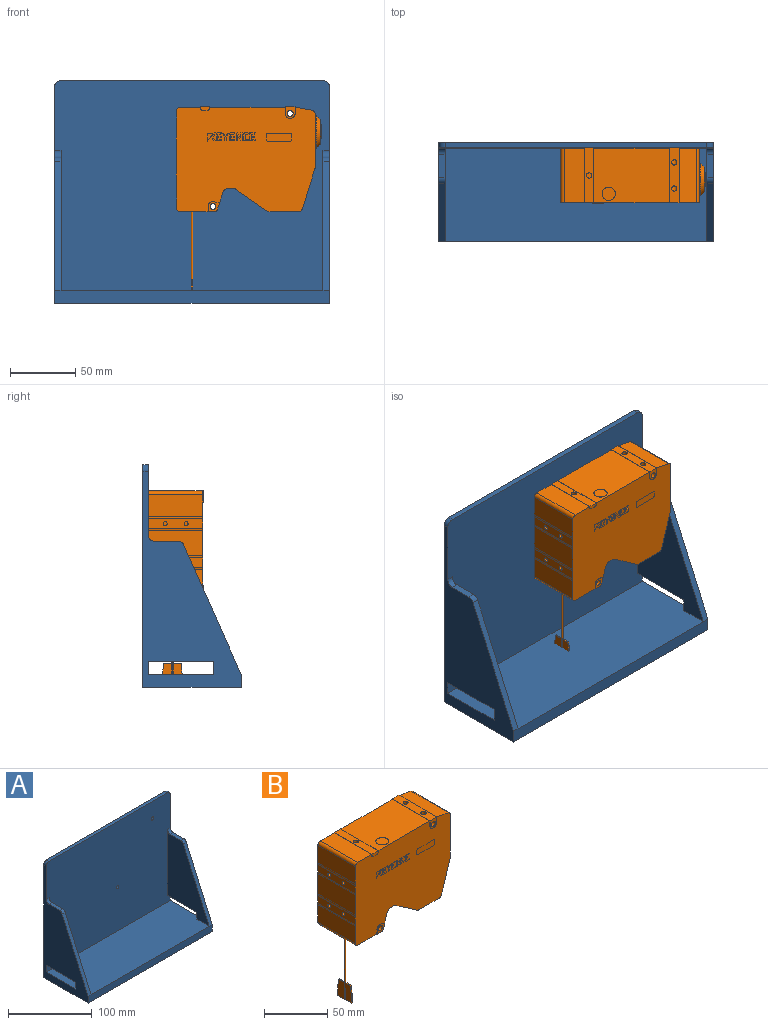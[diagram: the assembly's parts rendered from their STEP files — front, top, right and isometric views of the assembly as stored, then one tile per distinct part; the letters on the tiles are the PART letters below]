
ASSEMBLY  parts=2 mates=1
PART A: 26 faces, bbox 210x75x170 mm
  f0: plane 210x71mm, normal (0,0,1), area 14700mm2, adj f1,f3,f4,f5,f6,f11,f14,f16
  f1: plane 165x75mm, normal (1,0,0), area 5794.2mm2, adj f0,f6,f8,f11,f12,f15,f16,f17
  f2: plane 98.53x43.72mm, normal (0,-0.91,0.41), area 539mm2, adj f3,f4,f11,f23
  f3: plane 165x75mm, normal (-1,0,0), area 5794.2mm2, adj f0,f2,f6,f8,f11,f12,f13,f14
  f4: plane 106.5x71mm, normal (1,0,0), area 4424.2mm2, adj f0,f2,f6,f13,f14,f19,f22,f23
  f5: plane 106.5x71mm, normal (-1,0,0), area 4424.2mm2, adj f0,f6,f15,f16,f17,f18,f20,f21
  f6: plane 210x160mm, normal (0,-1,0), area 32593.9mm2, adj f0,f1,f3,f4,f5,f7,f9,f10
  f7: plane 200x4mm, normal (0,0,1), area 800mm2, adj f6,f8,f24,f25
  f8: plane 210x170mm, normal (0,1,0), area 35658.9mm2, adj f1,f3,f7,f9,f10,f12,f24,f25
  f9: cylinder r=2.2mm len=4.4mm, axis (0,-1,0), area 55.3mm2, adj f6,f8
  f10: cylinder r=2.2mm len=4.4mm, axis (0,-1,0), area 55.3mm2, adj f6,f8
  f11: plane 210x10mm, normal (0,-1,0), area 2100mm2, adj f0,f1,f2,f3,f12,f15
  f12: plane 210x75mm, normal (0,0,-1), area 15750mm2, adj f1,f3,f8,f11
  f13: plane 50x5mm, normal (0,0,-1), area 250mm2, adj f3,f4,f6,f14
  f14: plane 10x5mm, normal (0,1,0), area 50mm2, adj f0,f3,f4,f13
  f15: plane 98.53x43.72mm, normal (0,-0.91,0.41), area 539mm2, adj f1,f5,f11,f21
  f16: plane 10x5mm, normal (0,1,0), area 50mm2, adj f0,f1,f5,f17
  f17: plane 50x5mm, normal (0,0,-1), area 250mm2, adj f1,f5,f6,f16
  f18: plane 17.71x5mm, normal (0,0,1), area 88.5mm2, adj f1,f5,f20,f21
  f19: plane 17.71x5mm, normal (0,0,1), area 88.5mm2, adj f3,f4,f22,f23
  f20: cylinder r=5mm len=5mm, axis (-1,0,0), area 39.3mm2, adj f1,f5,f6,f18
  f21: cylinder r=5mm len=5mm, axis (1,0,0), area 28.8mm2, adj f1,f5,f15,f18
  f22: cylinder r=5mm len=5mm, axis (-1,0,0), area 39.3mm2, adj f3,f4,f6,f19
  f23: cylinder r=5mm len=5mm, axis (-1,0,0), area 28.8mm2, adj f2,f3,f4,f19
  f24: cylinder r=5mm len=5mm, axis (0,-1,0), area 31.4mm2, adj f1,f6,f7,f8
  f25: cylinder r=5mm len=5mm, axis (0,1,0), area 31.4mm2, adj f3,f6,f7,f8
PART B: 340 faces, bbox 111x42x148 mm
  f0: cone r=4.25mm half-angle=90deg, axis (-1,0,0), area 56.7mm2, adj f1
  f1: cylinder r=4.25mm len=8.5mm, axis (-1,0,0), area 106.8mm2, adj f0,f2
  f2: plane 9.5x9.5mm, normal (1,0,0), area 14.1mm2, adj f1,f10
  f3: plane 6.19x1mm, normal (0,0,1), area 6.1mm2, adj f4,f11,f12,f16
  f4: plane 8x1mm, normal (0,-1,0.09), area 8mm2, adj f3,f5,f11,f12
  f5: plane 8x1mm, normal (0,-1,0), area 8mm2, adj f4,f8,f11,f12
  f6: plane 8x1mm, normal (0,1,0.09), area 8mm2, adj f7,f9,f13,f14
  f7: plane 6.19x1mm, normal (0,0,1), area 6.1mm2, adj f6,f13,f14,f17
  f8: plane 15x1.5mm, normal (0,0,-1), area 15.4mm2, adj f5,f9,f11,f12,f13,f14,f16,f17
  f9: plane 8x1mm, normal (0,1,0), area 8mm2, adj f6,f8,f13,f14
  f10: cylinder r=4.75mm len=9.5mm, axis (-1,0,0), area 119.4mm2, adj f2,f15
  f11: plane 16x6.94mm, normal (1,0,0), area 108.1mm2, adj f3,f4,f5,f8,f16
  f12: plane 16x6.94mm, normal (-1,0,0), area 108.1mm2, adj f3,f4,f5,f8,f16
  f13: plane 16x6.94mm, normal (-1,0,0), area 108.1mm2, adj f6,f7,f8,f9,f17
  f14: plane 16x6.94mm, normal (1,0,0), area 108.1mm2, adj f6,f7,f8,f9,f17
  f15: plane 10.5x10.5mm, normal (1,0,0), area 15.7mm2, adj f10,f19
  f16: cylinder r=0.75mm len=68.1mm, axis (0,0,-1), area 142.9mm2, adj f3,f8,f11,f12,f17,f20
  f17: cylinder r=0.75mm len=68.1mm, axis (0,0,-1), area 142.9mm2, adj f7,f8,f13,f14,f16,f20
  f18: plane 16x13.11mm, normal (-0.57,0,-0.82), area 201.1mm2, adj f21
  f19: cone r=5.25mm half-angle=0deg, axis (1,0,0), area 131.9mm2, adj f15,f22
  f20: plane 15x3mm, normal (0,0,-1), area 43.2mm2, adj f16,f17,f23,f24,f25,f26
  f21: cylinder r=8mm len=16mm, axis (-0.57,0,-0.82), area 5mm2, adj f18,f27
  f22: cone r=8.5mm half-angle=90deg, axis (-1,0,0), area 140.4mm2, adj f19,f28
  f23: plane 15x0.1mm, normal (-1,0,0), area 1.5mm2, adj f20,f24,f26,f30
  f24: plane 3x0.1mm, normal (0,1,0), area 0.3mm2, adj f20,f23,f25,f30
  f25: plane 15x0.1mm, normal (1,0,0), area 1.5mm2, adj f20,f24,f26,f30
  f26: plane 3x0.1mm, normal (0,-1,0), area 0.3mm2, adj f20,f23,f25,f30
  f27: plane 19.8x16.22mm, normal (-0.57,0,-0.82), area 191mm2, adj f21,f31,f32,f33,f34
  f28: cylinder r=8.5mm len=17mm, axis (-1,0,0), area 160.2mm2, adj f22,f35
  f29: plane 4x4mm, normal (0,0,1), area 12.6mm2, adj f36
  f30: plane 19.8x13.8mm, normal (0,0,-1), area 228.2mm2, adj f23,f24,f25,f26,f37,f38,f39,f40
  f31: plane 19.8x0.08mm, normal (0.82,0,-0.57), area 2mm2, adj f27,f32,f34,f51
  f32: plane 16.28x11.44mm, normal (0,1,0), area 2mm2, adj f27,f31,f33,f51
  f33: plane 19.8x0.08mm, normal (-0.82,0,0.57), area 2mm2, adj f27,f32,f34,f51
  f34: plane 16.28x11.44mm, normal (0,-1,0), area 2mm2, adj f27,f31,f33,f51
  f35: plane 19x19mm, normal (1,0,0), area 56.5mm2, adj f28,f52
  f36: cylinder r=2mm len=4.2mm, axis (0,0,1), area 52.8mm2, adj f29,f57
  f37: plane 19.8x0.1mm, normal (1,0,0), area 2mm2, adj f30,f38,f40,f62
  f38: plane 13.8x0.1mm, normal (0,1,0), area 1.4mm2, adj f30,f37,f39,f62
  f39: plane 19.8x0.1mm, normal (-1,0,0), area 2mm2, adj f30,f38,f40,f62
  f40: plane 13.8x0.1mm, normal (0,-1,0), area 1.4mm2, adj f30,f37,f39,f62
  f41: plane 6.97x2.98mm, normal (0,-1,0), area 19.1mm2, adj f57,f66,f67,f68,f185,f189
  f42: plane 19.1x5.6mm, normal (0,-1,0), area 106.5mm2, adj f69,f70,f71,f72,f73,f74,f75,f76
  f43: plane 5.91x4.22mm, normal (0,-1,0), area 12.8mm2, adj f77,f78,f79,f80,f81,f82,f83,f84
  f44: plane 6.17x4.28mm, normal (0,-1,0), area 12.9mm2, adj f89,f90,f91,f92
  f45: plane 5.92x4.29mm, normal (0,-1,0), area 16mm2, adj f93,f94,f95,f96,f97,f98,f99,f100
  f46: plane 5.92x4.29mm, normal (0,-1,0), area 16mm2, adj f109,f110,f111,f112,f113,f114,f115,f116
  f47: plane 5.96x4.36mm, normal (0,-1,0), area 16.6mm2, adj f125,f126,f127,f128,f129,f130,f131,f132
  f48: plane 5.9x3.51mm, normal (0,-1,0), area 8mm2, adj f141,f142,f143,f144,f145,f146
  f49: plane 5.91x4.97mm, normal (0,-1,0), area 8.9mm2, adj f147,f148,f149,f150,f151,f152,f153,f154
  f50: plane 5.91x4.74mm, normal (0,-1,0), area 18.3mm2, adj f156,f157,f158,f159,f160,f161,f162,f163
  f51: plane 20x16.38mm, normal (-0.57,0,-0.82), area 8mm2, adj f31,f32,f33,f34,f174,f175,f176,f177
  f52: cone r=12.5mm half-angle=45deg, axis (-1,0,0), area 293.2mm2, adj f35,f179
  f53: cylinder r=2mm len=4.08mm, axis (0,0,1), area 42.4mm2, adj f55,f181
  f54: cylinder r=2mm len=4.08mm, axis (0,0,1), area 42.4mm2, adj f55,f181
  f55: cylinder r=2.2mm len=42mm, axis (0,1,0), area 551.2mm2, adj f53,f54,f182,f184
  f56: plane 10.12x10.12mm, normal (0,0,1), area 80.4mm2, adj f187
  f57: plane 42x6.97mm, normal (0,0,1), area 280mm2, adj f36,f41,f185,f188,f189
  f58: plane 3x3mm, normal (-1,0,0), area 7.1mm2, adj f191
  f59: plane 3x3mm, normal (-1,0,0), area 7.1mm2, adj f192
  f60: plane 3x3mm, normal (-1,0,0), area 7.1mm2, adj f195
  f61: plane 3x3mm, normal (-1,0,0), area 7.1mm2, adj f196
  f62: plane 20x14mm, normal (0,0,-1), area 6.8mm2, adj f37,f38,f39,f40,f198,f199,f200,f201
  f63: cylinder r=3.73mm len=7.47mm, axis (0,1,0), area 2.3mm2, adj f64,f182,f202,f258
  f64: plane 4.8x0.2mm, normal (-1,0,0), area 1mm2, adj f63,f65,f182,f202
  f65: plane 0.2x0mm, normal (0,0,-1), area 0mm2, adj f64,f182,f186,f202
  f66: cylinder r=1.98mm len=1.98mm, axis (0,1,0), area 0.6mm2, adj f41,f67,f185,f202
  f67: plane 3x0.2mm, normal (0,0,-1), area 0.6mm2, adj f41,f66,f68,f202
  f68: cylinder r=1.98mm len=1.98mm, axis (0,1,0), area 0.6mm2, adj f41,f67,f189,f202
  f69: cylinder r=0.7mm len=0.7mm, axis (0,-1,0), area 0mm2, adj f42,f70,f76,f202
  f70: plane 17.7x0.01mm, normal (0,0,-1), area 0.2mm2, adj f42,f69,f71,f202
  f71: cylinder r=0.7mm len=0.7mm, axis (0,-1,0), area 0mm2, adj f42,f70,f72,f202
  f72: plane 4.2x0.01mm, normal (-1,0,0), area 0mm2, adj f42,f71,f73,f202
  f73: cylinder r=0.7mm len=0.7mm, axis (0,-1,0), area 0mm2, adj f42,f72,f74,f202
  f74: plane 17.7x0.01mm, normal (0,0,1), area 0.2mm2, adj f42,f73,f75,f202
  f75: cylinder r=0.7mm len=0.7mm, axis (0,-1,0), area 0mm2, adj f42,f74,f76,f202
  f76: plane 4.2x0.01mm, normal (1,0,0), area 0mm2, adj f42,f69,f75,f202
  f77: extruded ~0.48x0.26mm, area 0mm2, adj f43,f78,f88,f202
  f78: plane 2.6x0.01mm, normal (1,0,0), area 0mm2, adj f43,f77,f79,f202
  f79: extruded ~0.48x0.26mm, area 0mm2, adj f43,f78,f80,f202
  f80: plane 2.78x0.01mm, normal (0,0,1), area 0mm2, adj f43,f79,f81,f202
  f81: plane 1.17x0.01mm, normal (1,0,0), area 0mm2, adj f43,f80,f82,f202
  f82: plane 3.35x0.01mm, normal (0,0,-1), area 0mm2, adj f43,f81,f83,f202
  f83: extruded ~1.51x0.82mm, area 0mm2, adj f43,f82,f84,f202
  f84: plane 2.89x0.01mm, normal (-1,0,0), area 0mm2, adj f43,f83,f85,f202
  f85: extruded ~1.5x0.82mm, area 0mm2, adj f43,f84,f86,f202
  f86: plane 3.4x0.01mm, normal (0,0,1), area 0mm2, adj f43,f85,f87,f202
  f87: cylinder r=2846.98mm len=1.16mm, axis (0,1,0), area 0mm2, adj f43,f86,f88,f202
  f88: plane 1.95x0.01mm, normal (0,0,-1), area 0mm2, adj f43,f77,f87,f202
  f89: extruded ~1.5x0.82mm, area 0mm2, adj f44,f90,f92,f202
  f90: plane 3.45x0.01mm, normal (0,0,1), area 0mm2, adj f44,f89,f91,f202
  f91: extruded ~6.17x4.27mm, area 0.1mm2, adj f44,f90,f92,f202
  f92: plane 4.66x0.01mm, normal (-1,0,0), area 0mm2, adj f44,f89,f91,f202
  f93: extruded ~1.5x0.82mm, area 0mm2, adj f45,f94,f108,f202
  f94: plane 3.47x0.01mm, normal (0,0,1), area 0mm2, adj f45,f93,f95,f202
  f95: cylinder r=2856.37mm len=1.16mm, axis (0,1,0), area 0mm2, adj f45,f94,f96,f202
  f96: plane 1.98x0.01mm, normal (0,0,-1), area 0mm2, adj f45,f95,f97,f202
  f97: extruded ~0.48x0.26mm, area 0mm2, adj f45,f96,f98,f202
  f98: plane 0.81x0.01mm, normal (1,0,0), area 0mm2, adj f45,f97,f99,f202
  f99: plane 2.84x0.01mm, normal (0,0,1), area 0mm2, adj f45,f98,f100,f202
  f100: plane 0.99x0.01mm, normal (1,0,0), area 0mm2, adj f45,f99,f101,f202
  f101: plane 2.84x0.01mm, normal (0,0,-1), area 0mm2, adj f45,f100,f102,f202
  f102: plane 0.81x0.01mm, normal (1,0,0), area 0mm2, adj f45,f101,f103,f202
  f103: extruded ~0.5x0.27mm, area 0mm2, adj f45,f102,f104,f202
  f104: plane 2.8x0.01mm, normal (0,0,1), area 0mm2, adj f45,f103,f105,f202
  f105: plane 1.16x0.01mm, normal (1,0,0), area 0mm2, adj f45,f104,f106,f202
  f106: plane 3.44x0.01mm, normal (0,0,-1), area 0mm2, adj f45,f105,f107,f202
  f107: extruded ~1.5x0.81mm, area 0mm2, adj f45,f106,f108,f202
  f108: plane 2.9x0.01mm, normal (-1,0,0), area 0mm2, adj f45,f93,f107,f202
  f109: extruded ~0.5x0.27mm, area 0mm2, adj f46,f110,f124,f202
  f110: plane 2.8x0.01mm, normal (0,0,1), area 0mm2, adj f46,f109,f111,f202
  f111: plane 1.16x0.01mm, normal (1,0,0), area 0mm2, adj f46,f110,f112,f202
  f112: plane 3.44x0.01mm, normal (0,0,-1), area 0mm2, adj f46,f111,f113,f202
  f113: extruded ~1.5x0.81mm, area 0mm2, adj f46,f112,f114,f202
  f114: plane 2.9x0.01mm, normal (-1,0,0), area 0mm2, adj f46,f113,f115,f202
  f115: extruded ~1.5x0.82mm, area 0mm2, adj f46,f114,f116,f202
  f116: plane 3.47x0.01mm, normal (0,0,1), area 0mm2, adj f46,f115,f117,f202
  f117: cylinder r=2855.24mm len=1.16mm, axis (0,1,0), area 0mm2, adj f46,f116,f118,f202
  f118: plane 1.98x0.01mm, normal (0,0,-1), area 0mm2, adj f46,f117,f119,f202
  f119: extruded ~0.48x0.26mm, area 0mm2, adj f46,f118,f120,f202
  f120: plane 0.81x0.01mm, normal (1,0,0), area 0mm2, adj f46,f119,f121,f202
  f121: plane 2.84x0.01mm, normal (0,0,1), area 0mm2, adj f46,f120,f122,f202
  f122: plane 0.99x0.01mm, normal (1,0,0), area 0mm2, adj f46,f121,f123,f202
  f123: plane 2.84x0.01mm, normal (0,0,-1), area 0mm2, adj f46,f122,f124,f202
  f124: plane 0.81x0.01mm, normal (1,0,0), area 0mm2, adj f46,f109,f123,f202
  f125: extruded ~1.53x0.84mm, area 0mm2, adj f47,f126,f140,f202
  f126: plane 3.51x0.01mm, normal (0,0,1), area 0mm2, adj f47,f125,f127,f202
  f127: cylinder r=2853.49mm len=1.2mm, axis (0,1,0), area 0mm2, adj f47,f126,f128,f202
  f128: plane 1.99x0.01mm, normal (0,0,-1), area 0mm2, adj f47,f127,f129,f202
  f129: extruded ~0.46x0.24mm, area 0mm2, adj f47,f128,f130,f202
  f130: plane 0.78x0.01mm, normal (1,0,0), area 0mm2, adj f47,f129,f131,f202
  f131: plane 2.84x0.01mm, normal (0,0,1), area 0mm2, adj f47,f130,f132,f202
  f132: plane 1.03x0.01mm, normal (1,0,0), area 0mm2, adj f47,f131,f133,f202
  f133: plane 2.84x0.01mm, normal (0,0,-1), area 0mm2, adj f47,f132,f134,f202
  f134: plane 0.79x0.01mm, normal (1,0,0), area 0mm2, adj f47,f133,f135,f202
  f135: extruded ~0.48x0.25mm, area 0mm2, adj f47,f134,f136,f202
  f136: plane 2.83x0.01mm, normal (0,0,1), area 0mm2, adj f47,f135,f137,f202
  f137: plane 1.2x0.01mm, normal (1,0,0), area 0mm2, adj f47,f136,f138,f202
  f138: plane 3.46x0.01mm, normal (0,0,-1), area 0mm2, adj f47,f137,f139,f202
  f139: extruded ~1.53x0.84mm, area 0mm2, adj f47,f138,f140,f202
  f140: plane 2.9x0.01mm, normal (-1,0,0), area 0mm2, adj f47,f125,f139,f202
  f141: plane 1.32x0.01mm, normal (0,0,1), area 0mm2, adj f48,f142,f146,f202
  f142: cylinder r=2917.35mm len=2.86mm, axis (0,1,0), area 0mm2, adj f48,f141,f143,f202
  f143: cylinder r=3224.09mm len=3.04mm, axis (0,-1,0), area 0mm2, adj f48,f142,f144,f202
  f144: plane 1.37x0.01mm, normal (0,0,-1), area 0mm2, adj f48,f143,f145,f202
  f145: cylinder r=3203.54mm len=2.96mm, axis (0,1,0), area 0mm2, adj f48,f144,f146,f202
  f146: cylinder r=2923.49mm len=2.95mm, axis (0,-1,0), area 0mm2, adj f48,f141,f145,f202
  f147: plane 2.87x0.01mm, normal (-1,0,0), area 0mm2, adj f49,f148,f155,f202
  f148: cylinder r=2953.73mm len=3.04mm, axis (0,1,0), area 0mm2, adj f49,f147,f149,f202
  f149: plane 0.97x0.01mm, normal (0,0,1), area 0mm2, adj f49,f148,f150,f202
  f150: cylinder r=2922.38mm len=2.34mm, axis (0,-1,0), area 0mm2, adj f49,f149,f151,f202
  f151: cylinder r=2921.52mm len=2.34mm, axis (0,-1,0), area 0mm2, adj f49,f150,f152,f202
  f152: plane 0.97x0.01mm, normal (0,0,1), area 0mm2, adj f49,f151,f153,f202
  f153: cylinder r=2953.58mm len=3.04mm, axis (0,1,0), area 0mm2, adj f49,f152,f154,f202
  f154: plane 2.87x0.01mm, normal (1,0,0), area 0mm2, adj f49,f153,f155,f202
  f155: plane 1.11x0.01mm, normal (0,0,-1), area 0mm2, adj f49,f147,f154,f202
  f156: plane 3.55x0.01mm, normal (-1,0,0), area 0mm2, adj f50,f157,f165,f202
  f157: plane 1.12x0.01mm, normal (0,0,1), area 0mm2, adj f50,f156,f158,f202
  f158: plane 5.91x0.01mm, normal (1,0,0), area 0.1mm2, adj f50,f157,f159,f202
  f159: plane 1.02x0.01mm, normal (0,0,-1), area 0mm2, adj f50,f158,f160,f202
  f160: cylinder r=3134.07mm len=3.98mm, axis (0,1,0), area 0mm2, adj f50,f159,f161,f202
  f161: plane 3.99x0.01mm, normal (1,0,0), area 0mm2, adj f50,f160,f162,f202
  f162: plane 1.12x0.01mm, normal (0,0,-1), area 0mm2, adj f50,f161,f163,f202
  f163: plane 5.91x0.01mm, normal (-1,0,0), area 0.1mm2, adj f50,f162,f164,f202
  f164: plane 1.09x0.01mm, normal (0,0,1), area 0mm2, adj f50,f163,f165,f202
  f165: cylinder r=2944.12mm len=3.55mm, axis (0,-1,0), area 0mm2, adj f50,f156,f164,f202
  f166: plane 3.81x1.2mm, normal (0.3,0,0.95), area 0.8mm2, adj f167,f202,f203,f247
  f167: cylinder r=3.73mm len=4.86mm, axis (0,1,0), area 1.4mm2, adj f166,f168,f202,f203
  f168: plane 4x0.2mm, normal (-1,0,0), area 0.8mm2, adj f167,f202,f203,f274
  f169: cylinder r=2.2mm len=42mm, axis (0,1,0), area 580.6mm2, adj f203,f205
  f170: plane 5.96x4.36mm, normal (0,1,0), area 16.6mm2, adj f211,f212,f213,f214,f215,f216,f217,f218
  f171: plane 5.9x3.51mm, normal (0,1,0), area 8mm2, adj f227,f228,f229,f230,f231,f232
  f172: plane 6.17x4.28mm, normal (0,1,0), area 12.9mm2, adj f233,f234,f235,f236
  f173: plane 19.1x5.6mm, normal (0,1,0), area 106.5mm2, adj f237,f238,f239,f240,f241,f242,f243,f244
  f174: plane 20x0.08mm, normal (-0.82,0,0.57), area 2mm2, adj f51,f175,f177,f251
  f175: plane 16.44x11.55mm, normal (0,1,0), area 2mm2, adj f51,f174,f176,f251
  f176: plane 20x0.08mm, normal (0.82,0,-0.57), area 2mm2, adj f51,f175,f177,f251
  f177: plane 16.44x11.55mm, normal (0,-1,0), area 2mm2, adj f51,f174,f176,f251
  f178: cylinder r=2.7mm len=41.6mm, axis (0,1,0), area 68.6mm2, adj f202,f251,f252,f339
  f179: cylinder r=12.5mm len=25mm, axis (-1,0,0), area 78.5mm2, adj f52,f255
  f180: cylinder r=2.7mm len=41.6mm, axis (0,1,0), area 34.3mm2, adj f202,f254,f255,f339
  f181: plane 42x7.47mm, normal (0,0,1), area 288.5mm2, adj f53,f54,f182,f184,f186,f258
  f182: plane 8.73x7.47mm, normal (0,-1,0), area 44mm2, adj f55,f63,f64,f65,f181,f186,f258
  f183: plane 41.6x0.02mm, normal (0,0,1), area 0.7mm2, adj f202,f257,f258,f339
  f184: plane 8.73x7.47mm, normal (0,1,0), area 44mm2, adj f55,f181,f186,f258,f259,f260,f261
  f185: plane 42x1mm, normal (1,0,0), area 8.7mm2, adj f41,f57,f66,f188,f202,f262,f263,f339
  f186: plane 42x0.2mm, normal (-1,0,0), area 8.4mm2, adj f65,f181,f182,f184,f261,f262
  f187: cylinder r=5.06mm len=10.12mm, axis (0,0,1), area 3.2mm2, adj f56,f262
  f188: plane 6.97x2.98mm, normal (0,1,0), area 19.1mm2, adj f57,f185,f189,f263,f264,f265
  f189: plane 42x1mm, normal (-1,0,0), area 8.7mm2, adj f41,f57,f68,f188,f202,f265,f266,f339
  f190: cylinder r=5.91mm len=41.6mm, axis (0,1,0), area 64.7mm2, adj f202,f268,f269,f339
  f191: cylinder r=1.5mm len=3.5mm, axis (-1,0,0), area 33mm2, adj f58,f269
  f192: cylinder r=1.5mm len=3.5mm, axis (-1,0,0), area 33mm2, adj f59,f269
  f193: cylinder r=5.91mm len=41.6mm, axis (0,1,0), area 64.7mm2, adj f202,f269,f270,f339
  f194: cylinder r=5.91mm len=41.6mm, axis (0,1,0), area 64.7mm2, adj f202,f270,f271,f339
  f195: cylinder r=1.5mm len=3.5mm, axis (-1,0,0), area 33mm2, adj f60,f271
  f196: cylinder r=1.5mm len=3.5mm, axis (-1,0,0), area 33mm2, adj f61,f271
  f197: cylinder r=5.91mm len=41.6mm, axis (0,1,0), area 64.7mm2, adj f202,f271,f272,f339
  f198: plane 20x0.1mm, normal (-1,0,0), area 2mm2, adj f62,f199,f201,f274
  f199: plane 14x0.1mm, normal (0,1,0), area 1.4mm2, adj f62,f198,f200,f274
  f200: plane 20x0.1mm, normal (1,0,0), area 2mm2, adj f62,f199,f201,f274
  f201: plane 14x0.1mm, normal (0,-1,0), area 1.4mm2, adj f62,f198,f200,f274
  f202: plane 106.01x79.81mm, normal (0,-1,0), area 7485.2mm2, adj f63,f64,f65,f66,f67,f68,f69,f70
  f203: plane 8.67x7.73mm, normal (0,-1,0), area 38.7mm2, adj f166,f167,f168,f169,f204,f247,f274
  f204: cylinder r=2.7mm len=42mm, axis (0,1,0), area 143.5mm2, adj f203,f205,f247,f274
  f205: plane 8.67x7.73mm, normal (0,1,0), area 38.7mm2, adj f169,f204,f245,f246,f247,f274,f275
  f206: plane 5.91x4.22mm, normal (0,1,0), area 12.8mm2, adj f276,f277,f278,f279,f280,f281,f282,f283
  f207: plane 5.92x4.29mm, normal (0,1,0), area 16mm2, adj f288,f289,f290,f291,f292,f293,f294,f295
  f208: plane 5.91x4.74mm, normal (0,1,0), area 18.3mm2, adj f304,f305,f306,f307,f308,f309,f310,f311
  f209: plane 5.91x4.97mm, normal (0,1,0), area 8.9mm2, adj f314,f315,f316,f317,f318,f319,f320,f321
  f210: plane 5.92x4.29mm, normal (0,1,0), area 16mm2, adj f323,f324,f325,f326,f327,f328,f329,f330
  f211: extruded ~0.48x0.25mm, area 0mm2, adj f170,f212,f226,f339
  f212: plane 0.79x0.01mm, normal (-1,0,0), area 0mm2, adj f170,f211,f213,f339
  f213: plane 2.84x0.01mm, normal (0,0,-1), area 0mm2, adj f170,f212,f214,f339
  f214: plane 1.03x0.01mm, normal (-1,0,0), area 0mm2, adj f170,f213,f215,f339
  f215: plane 2.84x0.01mm, normal (0,0,1), area 0mm2, adj f170,f214,f216,f339
  f216: plane 0.78x0.01mm, normal (-1,0,0), area 0mm2, adj f170,f215,f217,f339
  f217: extruded ~0.46x0.24mm, area 0mm2, adj f170,f216,f218,f339
  f218: plane 1.99x0.01mm, normal (0,0,-1), area 0mm2, adj f170,f217,f219,f339
  f219: cylinder r=2853.49mm len=1.2mm, axis (0,-1,0), area 0mm2, adj f170,f218,f220,f339
  f220: plane 3.51x0.01mm, normal (0,0,1), area 0mm2, adj f170,f219,f221,f339
  f221: extruded ~1.53x0.84mm, area 0mm2, adj f170,f220,f222,f339
  f222: plane 2.9x0.01mm, normal (1,0,0), area 0mm2, adj f170,f221,f223,f339
  f223: extruded ~1.53x0.84mm, area 0mm2, adj f170,f222,f224,f339
  f224: plane 3.46x0.01mm, normal (0,0,-1), area 0mm2, adj f170,f223,f225,f339
  f225: plane 1.2x0.01mm, normal (-1,0,0), area 0mm2, adj f170,f224,f226,f339
  f226: plane 2.83x0.01mm, normal (0,0,1), area 0mm2, adj f170,f211,f225,f339
  f227: cylinder r=2917.35mm len=2.86mm, axis (0,-1,0), area 0mm2, adj f171,f228,f232,f339
  f228: plane 1.32x0.01mm, normal (0,0,1), area 0mm2, adj f171,f227,f229,f339
  f229: cylinder r=2923.49mm len=2.95mm, axis (0,1,0), area 0mm2, adj f171,f228,f230,f339
  f230: cylinder r=3203.54mm len=2.96mm, axis (0,-1,0), area 0mm2, adj f171,f229,f231,f339
  f231: plane 1.37x0.01mm, normal (0,0,-1), area 0mm2, adj f171,f230,f232,f339
  f232: cylinder r=3224.09mm len=3.04mm, axis (0,1,0), area 0mm2, adj f171,f227,f231,f339
  f233: extruded ~6.17x4.27mm, area 0.1mm2, adj f172,f234,f236,f339
  f234: plane 3.45x0.01mm, normal (0,0,1), area 0mm2, adj f172,f233,f235,f339
  f235: extruded ~1.5x0.82mm, area 0mm2, adj f172,f234,f236,f339
  f236: plane 4.66x0.01mm, normal (1,0,0), area 0mm2, adj f172,f233,f235,f339
  f237: plane 17.7x0.01mm, normal (0,0,-1), area 0.2mm2, adj f173,f238,f244,f339
  f238: cylinder r=0.7mm len=0.7mm, axis (0,1,0), area 0mm2, adj f173,f237,f239,f339
  f239: plane 4.2x0.01mm, normal (-1,0,0), area 0mm2, adj f173,f238,f240,f339
  f240: cylinder r=0.7mm len=0.7mm, axis (0,1,0), area 0mm2, adj f173,f239,f241,f339
  f241: plane 17.7x0.01mm, normal (0,0,1), area 0.2mm2, adj f173,f240,f242,f339
  f242: cylinder r=0.7mm len=0.7mm, axis (0,1,0), area 0mm2, adj f173,f241,f243,f339
  f243: plane 4.2x0.01mm, normal (1,0,0), area 0mm2, adj f173,f242,f244,f339
  f244: cylinder r=0.7mm len=0.7mm, axis (0,1,0), area 0mm2, adj f173,f237,f243,f339
  f245: cylinder r=3.73mm len=4.86mm, axis (0,-1,0), area 1.4mm2, adj f205,f246,f275,f339
  f246: plane 3.81x1.2mm, normal (0.3,0,0.95), area 0.8mm2, adj f205,f245,f247,f339
  f247: plane 42x12.62mm, normal (0.95,0,-0.3), area 552.1mm2, adj f166,f202,f203,f204,f205,f246,f248,f339
  f248: cylinder r=5mm len=41.6mm, axis (0,1,0), area 263.2mm2, adj f202,f247,f249,f339
  f249: plane 41.6x2.39mm, normal (0,0,-1), area 99.4mm2, adj f202,f248,f250,f339
  f250: cylinder r=5mm len=41.6mm, axis (0,1,0), area 127.1mm2, adj f202,f249,f251,f339
  f251: plane 41.6x23.72mm, normal (-0.57,0,-0.82), area 804.5mm2, adj f174,f175,f176,f177,f178,f202,f250,f339
  f252: plane 41.6x22.82mm, normal (0,0,-1), area 949.2mm2, adj f178,f202,f253,f339
  f253: cylinder r=2.7mm len=41.6mm, axis (0,1,0), area 142.1mm2, adj f202,f252,f254,f339
  f254: plane 41.6x30.72mm, normal (0.95,0,-0.3), area 1339.8mm2, adj f180,f202,f253,f339
  f255: plane 41.6x41.34mm, normal (1,0,0), area 1228.7mm2, adj f179,f180,f202,f256,f339
  f256: cylinder r=2.7mm len=41.6mm, axis (0,1,0), area 156mm2, adj f202,f255,f257,f339
  f257: plane 41.6x13.04mm, normal (0.18,0,0.98), area 551.4mm2, adj f183,f202,f256,f339
  f258: plane 42x5mm, normal (1,0,0), area 10.3mm2, adj f63,f181,f182,f183,f184,f202,f259,f339
  f259: cylinder r=3.73mm len=7.47mm, axis (0,-1,0), area 2.3mm2, adj f184,f258,f260,f339
  f260: plane 4.8x0.2mm, normal (-1,0,0), area 1mm2, adj f184,f259,f261,f339
  f261: plane 0.2x0mm, normal (0,0,-1), area 0mm2, adj f184,f186,f260,f339
  f262: plane 57.78x41.6mm, normal (0,0,1), area 2323.4mm2, adj f185,f186,f187,f202,f339
  f263: cylinder r=1.98mm len=1.98mm, axis (0,-1,0), area 0.6mm2, adj f185,f188,f264,f339
  f264: plane 3x0.2mm, normal (0,0,-1), area 0.6mm2, adj f188,f263,f265,f339
  f265: cylinder r=1.98mm len=1.98mm, axis (0,-1,0), area 0.6mm2, adj f188,f189,f264,f339
  f266: plane 41.6x15.62mm, normal (0,0,1), area 649.7mm2, adj f189,f202,f267,f339
  f267: cylinder r=2.7mm len=41.6mm, axis (0,1,0), area 176.4mm2, adj f202,f266,f268,f339
  f268: plane 41.6x16.79mm, normal (-1,0,0), area 698.6mm2, adj f190,f202,f267,f339
  f269: plane 41.6x7.54mm, normal (-1,0,0), area 299.6mm2, adj f190,f191,f192,f193,f202,f339
  f270: plane 41.6x19.38mm, normal (-1,0,0), area 806.4mm2, adj f193,f194,f202,f339
  f271: plane 41.6x7.54mm, normal (-1,0,0), area 299.6mm2, adj f194,f195,f196,f197,f202,f339
  f272: plane 41.6x16.99mm, normal (-1,0,0), area 706.9mm2, adj f197,f202,f273,f339
  f273: cylinder r=2.7mm len=41.6mm, axis (0,1,0), area 176.4mm2, adj f202,f272,f274,f339
  f274: plane 42x26.05mm, normal (0,0,-1), area 805.7mm2, adj f168,f198,f199,f200,f201,f202,f203,f204
  f275: plane 4x0.2mm, normal (-1,0,0), area 0.8mm2, adj f205,f245,f274,f339
  f276: plane 3.4x0.01mm, normal (0,0,1), area 0mm2, adj f206,f277,f287,f339
  f277: extruded ~1.5x0.82mm, area 0mm2, adj f206,f276,f278,f339
  f278: plane 2.89x0.01mm, normal (1,0,0), area 0mm2, adj f206,f277,f279,f339
  f279: extruded ~1.51x0.82mm, area 0mm2, adj f206,f278,f280,f339
  f280: plane 3.35x0.01mm, normal (0,0,-1), area 0mm2, adj f206,f279,f281,f339
  f281: plane 1.17x0.01mm, normal (-1,0,0), area 0mm2, adj f206,f280,f282,f339
  f282: plane 2.78x0.01mm, normal (0,0,1), area 0mm2, adj f206,f281,f283,f339
  f283: extruded ~0.48x0.26mm, area 0mm2, adj f206,f282,f284,f339
  f284: plane 2.6x0.01mm, normal (-1,0,0), area 0mm2, adj f206,f283,f285,f339
  f285: extruded ~0.48x0.26mm, area 0mm2, adj f206,f284,f286,f339
  f286: plane 1.95x0.01mm, normal (0,0,-1), area 0mm2, adj f206,f285,f287,f339
  f287: cylinder r=2846.98mm len=1.16mm, axis (0,-1,0), area 0mm2, adj f206,f276,f286,f339
  f288: extruded ~1.5x0.82mm, area 0mm2, adj f207,f289,f303,f339
  f289: plane 2.9x0.01mm, normal (1,0,0), area 0mm2, adj f207,f288,f290,f339
  f290: extruded ~1.5x0.81mm, area 0mm2, adj f207,f289,f291,f339
  f291: plane 3.44x0.01mm, normal (0,0,-1), area 0mm2, adj f207,f290,f292,f339
  f292: plane 1.16x0.01mm, normal (-1,0,0), area 0mm2, adj f207,f291,f293,f339
  f293: plane 2.8x0.01mm, normal (0,0,1), area 0mm2, adj f207,f292,f294,f339
  f294: extruded ~0.5x0.27mm, area 0mm2, adj f207,f293,f295,f339
  f295: plane 0.81x0.01mm, normal (-1,0,0), area 0mm2, adj f207,f294,f296,f339
  f296: plane 2.84x0.01mm, normal (0,0,-1), area 0mm2, adj f207,f295,f297,f339
  f297: plane 0.99x0.01mm, normal (-1,0,0), area 0mm2, adj f207,f296,f298,f339
  f298: plane 2.84x0.01mm, normal (0,0,1), area 0mm2, adj f207,f297,f299,f339
  f299: plane 0.81x0.01mm, normal (-1,0,0), area 0mm2, adj f207,f298,f300,f339
  f300: extruded ~0.48x0.26mm, area 0mm2, adj f207,f299,f301,f339
  f301: plane 1.98x0.01mm, normal (0,0,-1), area 0mm2, adj f207,f300,f302,f339
  f302: cylinder r=2856.37mm len=1.16mm, axis (0,-1,0), area 0mm2, adj f207,f301,f303,f339
  f303: plane 3.47x0.01mm, normal (0,0,1), area 0mm2, adj f207,f288,f302,f339
  f304: plane 3.99x0.01mm, normal (-1,0,0), area 0mm2, adj f208,f305,f313,f339
  f305: cylinder r=3134.07mm len=3.98mm, axis (0,-1,0), area 0mm2, adj f208,f304,f306,f339
  f306: plane 1.02x0.01mm, normal (0,0,-1), area 0mm2, adj f208,f305,f307,f339
  f307: plane 5.91x0.01mm, normal (-1,0,0), area 0.1mm2, adj f208,f306,f308,f339
  f308: plane 1.12x0.01mm, normal (0,0,1), area 0mm2, adj f208,f307,f309,f339
  f309: plane 3.55x0.01mm, normal (1,0,0), area 0mm2, adj f208,f308,f310,f339
  f310: cylinder r=2944.12mm len=3.55mm, axis (0,1,0), area 0mm2, adj f208,f309,f311,f339
  f311: plane 1.09x0.01mm, normal (0,0,1), area 0mm2, adj f208,f310,f312,f339
  f312: plane 5.91x0.01mm, normal (1,0,0), area 0.1mm2, adj f208,f311,f313,f339
  f313: plane 1.12x0.01mm, normal (0,0,-1), area 0mm2, adj f208,f304,f312,f339
  f314: plane 2.87x0.01mm, normal (-1,0,0), area 0mm2, adj f209,f315,f322,f339
  f315: cylinder r=2953.58mm len=3.04mm, axis (0,-1,0), area 0mm2, adj f209,f314,f316,f339
  f316: plane 0.97x0.01mm, normal (0,0,1), area 0mm2, adj f209,f315,f317,f339
  f317: cylinder r=2921.52mm len=2.34mm, axis (0,1,0), area 0mm2, adj f209,f316,f318,f339
  f318: cylinder r=2922.38mm len=2.34mm, axis (0,1,0), area 0mm2, adj f209,f317,f319,f339
  f319: plane 0.97x0.01mm, normal (0,0,1), area 0mm2, adj f209,f318,f320,f339
  f320: cylinder r=2953.73mm len=3.04mm, axis (0,-1,0), area 0mm2, adj f209,f319,f321,f339
  f321: plane 2.87x0.01mm, normal (1,0,0), area 0mm2, adj f209,f320,f322,f339
  f322: plane 1.11x0.01mm, normal (0,0,-1), area 0mm2, adj f209,f314,f321,f339
  f323: plane 2.84x0.01mm, normal (0,0,1), area 0mm2, adj f210,f324,f338,f339
  f324: plane 0.81x0.01mm, normal (-1,0,0), area 0mm2, adj f210,f323,f325,f339
  f325: extruded ~0.48x0.26mm, area 0mm2, adj f210,f324,f326,f339
  f326: plane 1.98x0.01mm, normal (0,0,-1), area 0mm2, adj f210,f325,f327,f339
  f327: cylinder r=2855.24mm len=1.16mm, axis (0,-1,0), area 0mm2, adj f210,f326,f328,f339
  f328: plane 3.47x0.01mm, normal (0,0,1), area 0mm2, adj f210,f327,f329,f339
  f329: extruded ~1.5x0.82mm, area 0mm2, adj f210,f328,f330,f339
  f330: plane 2.9x0.01mm, normal (1,0,0), area 0mm2, adj f210,f329,f331,f339
  f331: extruded ~1.5x0.81mm, area 0mm2, adj f210,f330,f332,f339
  f332: plane 3.44x0.01mm, normal (0,0,-1), area 0mm2, adj f210,f331,f333,f339
  f333: plane 1.16x0.01mm, normal (-1,0,0), area 0mm2, adj f210,f332,f334,f339
  f334: plane 2.8x0.01mm, normal (0,0,1), area 0mm2, adj f210,f333,f335,f339
  f335: extruded ~0.5x0.27mm, area 0mm2, adj f210,f334,f336,f339
  f336: plane 0.81x0.01mm, normal (-1,0,0), area 0mm2, adj f210,f335,f337,f339
  f337: plane 2.84x0.01mm, normal (0,0,-1), area 0mm2, adj f210,f336,f338,f339
  f338: plane 0.99x0.01mm, normal (-1,0,0), area 0mm2, adj f210,f323,f337,f339
  f339: plane 106.01x79.81mm, normal (0,1,0), area 7485.2mm2, adj f178,f180,f183,f185,f189,f190,f193,f194
PLACE A rot(axis=(0,-1,0),0deg) t=(-80.23,-25.94,-15.05)mm
PLACE B rot(axis=(0,-1,0),0deg) t=(-80.23,-48.44,-95.05)mm
MATE fastened B.f55 <-> A.f9  axis (0,1,0) through (-5.23,-29.94,39.95)mm
